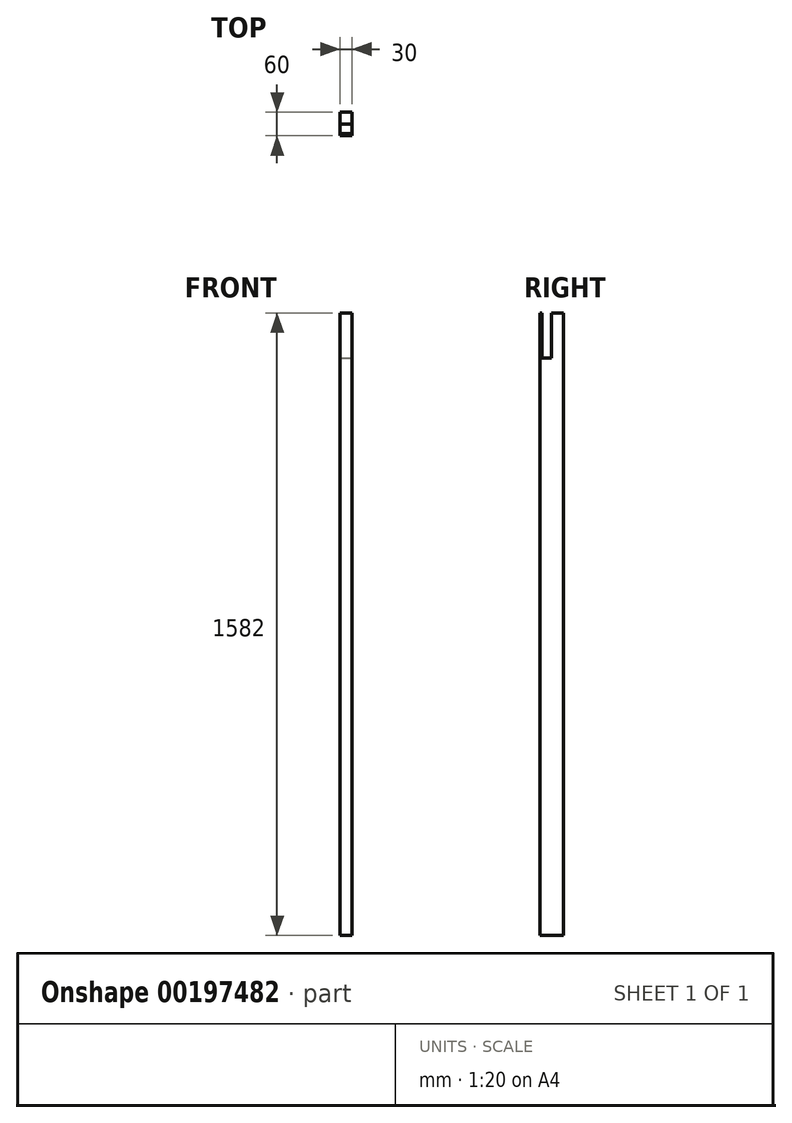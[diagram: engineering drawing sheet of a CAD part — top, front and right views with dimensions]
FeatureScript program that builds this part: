
annotation { "Feature Type Name" : "Feature", "Feature Type Description" : "" }
export const myFeature = defineFeature(function(context is Context, id is Id, definition is map)
    precondition{}
    {
        {
            var Q0;
            Q0=qCreatedBy(makeId("Right.planeOp"),FACE);
            var sketch = newSketch(context, id + "F0", { "sketchPlane" : qUnion([Q0])});
            skLineSegment(sketch, "E0.bottom", {"start": v(30, 791) * mm, "end": v(-30, 791) * mm});
            skLineSegment(sketch, "E0.top", {"start": v(30, -791) * mm, "end": v(-30, -791) * mm});
            skLineSegment(sketch, "E0.left", {"start": v(30, 791) * mm, "end": v(30, -791) * mm});
            skLineSegment(sketch, "E0.right", {"start": v(-30, 791) * mm, "end": v(-30, -791) * mm});
            skPoint(sketch, "E0.middle", {"position": v(0, 0) * mm});
            skSolve(sketch);
        }
        {
            var Q0;
            Q0 = qSketchRegion(id + "F0", true);
            extrude(context, id + "F1", {"entities" : qUnion([Q0]), "depth" : 30 * mm});
        }
        {
            var Q0;
            Q0=makeQuery(id+"F1.opExtrude","CAP_FACE",FACE,{"disambiguationData":[OSD([sQuery(id+"F0.wireOp",EDGE,"E0.bottom"),sQuery(id+"F0.wireOp",EDGE,"E0.top"),sQuery(id+"F0.wireOp",EDGE,"E0.left"),sQuery(id+"F0.wireOp",EDGE,"E0.right")])],"isStart":false});
            var sketch = newSketch(context, id + "F2", { "sketchPlane" : qUnion([Q0])});
            skLineSegment(sketch, "E1.bottom", {"start": v(-25, 676) * mm, "end": v(0, 676) * mm});
            skLineSegment(sketch, "E1.top", {"start": v(-25, 791) * mm, "end": v(0, 791) * mm});
            skLineSegment(sketch, "E1.left", {"start": v(-25, 676) * mm, "end": v(-25, 791) * mm});
            skLineSegment(sketch, "E1.right", {"start": v(0, 676) * mm, "end": v(0, 791) * mm});
            skSolve(sketch);
        }
        {
            var Q0;
            Q0 = qSketchRegion(id + "F2", true);
            extrude(context, id + "F3", {"entities" : qUnion([Q0]), "operationType" : NewBodyOperationType.REMOVE, "oppositeDirection" : true, "depth" : 30 * mm});
        }
    });
